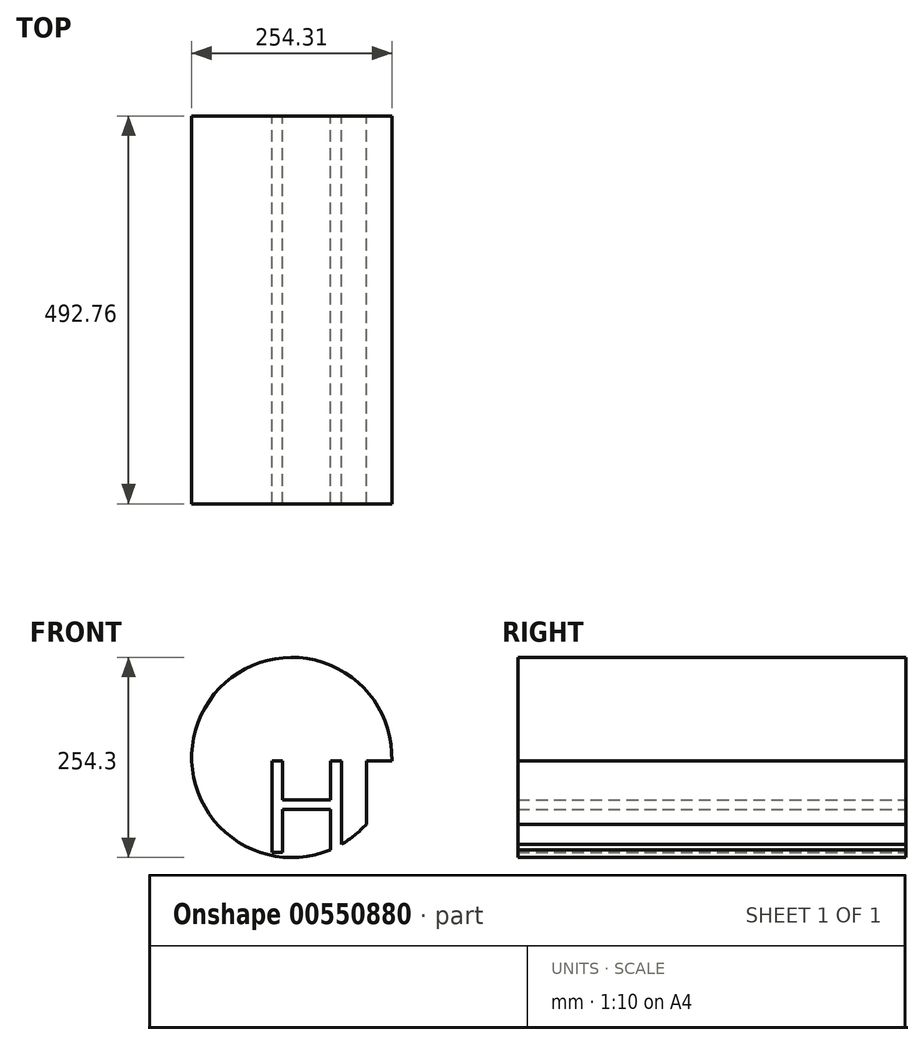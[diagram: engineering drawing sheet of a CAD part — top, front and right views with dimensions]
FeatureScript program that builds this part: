
annotation { "Feature Type Name" : "Feature", "Feature Type Description" : "" }
export const myFeature = defineFeature(function(context is Context, id is Id, definition is map)
    precondition{}
    {
        {
            var Q0;
            Q0=qCreatedBy(makeId("Front.planeOp"),FACE);
            var sketch = newSketch(context, id + "F0", { "sketchPlane" : qUnion([Q0])});
            skLineSegment(sketch, "E0.bottom", {"start": v(0, 0) * mm, "end": v(36.01, 0) * mm});
            skLineSegment(sketch, "E0.top", {"start": v(0, -55.28) * mm, "end": v(36.01, -55.28) * mm});
            skLineSegment(sketch, "E0.left", {"start": v(0, 0) * mm, "end": v(0, -55.28) * mm});
            skLineSegment(sketch, "E0.right", {"start": v(36.01, 0) * mm, "end": v(36.01, -55.28) * mm});
            skLineSegment(sketch, "E1.bottom", {"start": v(36.01, 0) * mm, "end": v(0, 0) * mm});
            skLineSegment(sketch, "E1.top", {"start": v(36.01, 63.88) * mm, "end": v(0, 63.88) * mm});
            skLineSegment(sketch, "E1.left", {"start": v(36.01, 0) * mm, "end": v(36.01, 63.88) * mm});
            skLineSegment(sketch, "E1.right", {"start": v(0, 0) * mm, "end": v(0, 63.88) * mm});
            skLineSegment(sketch, "E2.bottom", {"start": v(0, 63.88) * mm, "end": v(-28.53, 63.88) * mm});
            skLineSegment(sketch, "E2.top", {"start": v(0, 0) * mm, "end": v(-28.53, 0) * mm});
            skLineSegment(sketch, "E2.left", {"start": v(0, 63.88) * mm, "end": v(0, 0) * mm});
            skLineSegment(sketch, "E2.right", {"start": v(-28.53, 63.88) * mm, "end": v(-28.53, 0) * mm});
            skLineSegment(sketch, "E3.bottom", {"start": v(-28.53, 0) * mm, "end": v(0, 0) * mm});
            skLineSegment(sketch, "E3.top", {"start": v(-28.53, -55.28) * mm, "end": v(0, -55.28) * mm});
            skLineSegment(sketch, "E3.left", {"start": v(-28.53, 0) * mm, "end": v(-28.53, -55.28) * mm});
            skLineSegment(sketch, "E4", {"start": v(-28.53, 63.88) * mm, "end": v(-61.12, 63.88) * mm});
            skArc(sketch, "E5", {"start": v(-61.12, 63.88) * mm, "mid": v(-55.75, 90.95) * mm, "end": v(-71.05, 67.98) * mm});
            skLineSegment(sketch, "E6", {"start": v(-61.12, 77.95) * mm, "end": v(-58.32, 105.54) * mm});
            skLineSegment(sketch, "E7", {"start": v(-58.32, 105.54) * mm, "end": v(-22.27, 93.23) * mm});
            skLineSegment(sketch, "E8", {"start": v(-22.27, 93.23) * mm, "end": v(-52.27, 108.56) * mm});
            skLineSegment(sketch, "E9", {"start": v(-52.27, 108.56) * mm, "end": v(-59.18, 81.36) * mm});
            skLineSegment(sketch, "E10", {"start": v(-59.18, 81.36) * mm, "end": v(-31.98, 81.36) * mm});
            skLineSegment(sketch, "E11", {"start": v(-31.98, 81.36) * mm, "end": v(-28.1, 92.8) * mm});
            skLineSegment(sketch, "E12", {"start": v(-28.1, 92.8) * mm, "end": v(-46.37, 94.66) * mm});
            skLineSegment(sketch, "E13", {"start": v(-46.37, 94.66) * mm, "end": v(-46.37, 53.73) * mm});
            skCircle(sketch, "E14", {"center": v(-14.03, -224.66) * mm, "radius": 127.15 * mm});
            skCircle(sketch, "E15", {"center": v(-23.13, 115.9) * mm, "radius": 9.13 * mm});
            skCircle(sketch, "E16", {"center": v(6, 37.54) * mm, "radius": 119.9 * mm});
            skText(sketch, "E17", { "text": "HELLO\n\n", "fontName": "OpenSans-Regular.ttf"});
            const initialGuessF0  = {"E17": [-0.05513, -0.34498, 1, 0, 0.11702]};
            skSetInitialGuess(sketch, initialGuessF0);
            skSolve(sketch);
        }
        {
            var Q0;
            {var subQ9=sQuery(id+"F0.wireOp",EDGE,"E17.sketch_text.stroke-2");Q0=makeQuery(id+"F0.imprint","IMPRINT",FACE,{"disambiguationData":[TD([[makeQuery(id+"F0.imprint","IMPRINT",EDGE,{"derivedFrom":subQ9}),1.0]])]});}
            extrude(context, id + "F1", {"entities" : qUnion([Q0]), "depth" : 492.76 * mm, "offsetDistance" : 25.4 * mm});
        }
    });
